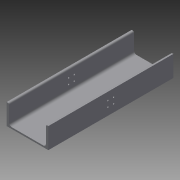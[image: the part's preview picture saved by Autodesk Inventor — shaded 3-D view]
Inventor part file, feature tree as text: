
AUTODESK INVENTOR PART (.ipt)
format: ipt  version: 2015 (Build 190159000, 159)  size: 117,248 bytes
history: native  units: in
note: dims shown in document units (in); Inventor stores cm internally (conversion verified against a paired STEP export)
features: sketch x2, extrude x1, hole x1
ambient origin geometry x8: Origin, YZ Plane, XZ Plane, XY Plane, X Axis, Y Axis, Z Axis, Center Point
bodies: Solid1 (feature_tree)
feature tree (4):
  extrude  "Extrusion1"  Depth=2.0in
  hole  "Hole2"  [1 undecoded]
  sketch  "Sketch1"  dims[d0=2.0in d1=2.0in]
  sketch  "Sketch3"  dims[d2=0.23in d3=1.85in d4=2.0in d5=0.23in d6=1.85in d7=2.0in d8=0.25in d9=0.25in d10=12.0in d11=0.0in d12=0.125in d13=0.125in d22=0.77in d23=0.144in d24=0.144in d25=0.144in d26=0.144in d31=0.15in d32=0.75in d33=0.279in d34=0.138in d35=0.5635in d36=1.0in d37=0.8108in]
note: 1 required parameter value undecoded (feature->parameter linkage not recoverable at this tier; creation-order binding heuristic only, values carry confidence <= 0.55)
